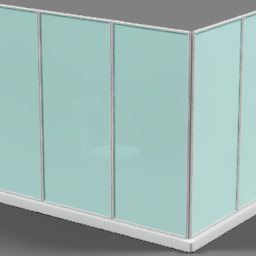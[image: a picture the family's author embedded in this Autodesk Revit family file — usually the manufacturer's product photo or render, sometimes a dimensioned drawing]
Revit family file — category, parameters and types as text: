
# Revit family: Layout-Teknion-Expansion_Cityline_Height_Adjustable_Workstation_09-R2021
name_source: partatom
category: Furniture Systems
units: mm (PartAtom-declared; Revit-internal decimal feet)

## family parameters
Always vertical = Yes
Cut with Voids When Loaded = No
OmniClass Number = 23.40.70.14.64.21
OmniClass Title = Systems Furniture
Part Type = Normal
Room Calculation Point = No
Round Connector Dimension = Use Diameter
Shared = Yes
Work Plane-Based = No

## types (1)
- Expansion Cityline Height-Adjustable Workstation 09
    Assembly Code = E2020200
    Default Elevation = 0 "
    Description = 12'-7" x 12'-0" Overall
    Manufacturer = Teknion
    Manufacturer Fax = 416.661.4586
    Model = Expansion Cityline Height-Adjustable Workstation Layout 09
    Product Line = Expansion Cityline
    Product Page URL = https://www.teknionplanningtool.com
    Series = Expansion Cityline
    Sustainability Data = https://www.teknion.com
    URL = www.teknion.com
    Unit Weight URL = http://www.teknion.com
    Warranty = http://www.teknion.com

## geometry (parser evidence)
native form markers: Blend x20, Sweep x36
no freeform markers — native parametric forms only
